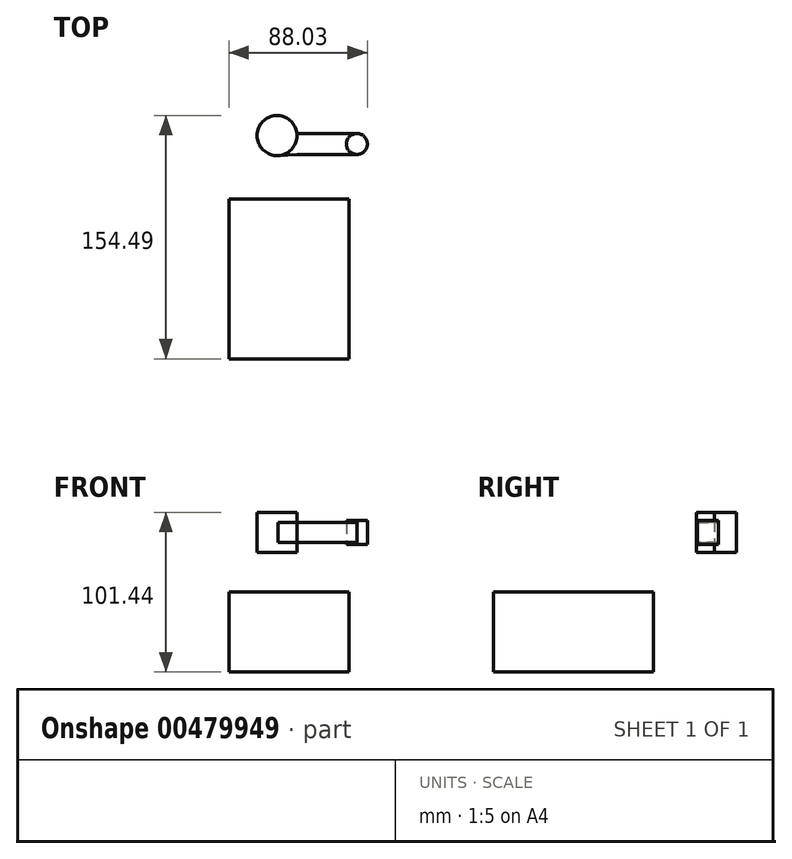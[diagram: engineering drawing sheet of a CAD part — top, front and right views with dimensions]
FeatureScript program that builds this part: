
annotation { "Feature Type Name" : "Feature", "Feature Type Description" : "" }
export const myFeature = defineFeature(function(context is Context, id is Id, definition is map)
    precondition{}
    {
        {
            var Q0;
            Q0=qCreatedBy(makeId("Front.planeOp"),FACE);
            var sketch = newSketch(context, id + "F0", { "sketchPlane" : qUnion([Q0])});
            skLineSegment(sketch, "E0.bottom", {"start": v(-76.2, -25.24) * mm, "end": v(0, -25.24) * mm});
            skLineSegment(sketch, "E0.top", {"start": v(-76.2, -76.04) * mm, "end": v(0, -76.04) * mm});
            skLineSegment(sketch, "E0.left", {"start": v(-76.2, -25.24) * mm, "end": v(-76.2, -76.04) * mm});
            skLineSegment(sketch, "E0.right", {"start": v(0, -25.24) * mm, "end": v(0, -76.04) * mm});
            skSolve(sketch);
        }
        {
            var Q0;
            Q0 = qSketchRegion(id + "F0", true);
            extrude(context, id + "F1", {"entities" : qUnion([Q0]), "depth" : 101.6 * mm});
        }
        {
            var Q0;
            Q0=qCreatedBy(makeId("Top.planeOp"),FACE);
            var sketch = newSketch(context, id + "F2", { "sketchPlane" : qUnion([Q0])});
            skCircle(sketch, "E1", {"center": v(-45.57, 40.19) * mm, "radius": 12.7 * mm});
            skLineSegment(sketch, "E2.bottom", {"start": v(-32.93, 41.47) * mm, "end": v(5.17, 41.47) * mm});
            skLineSegment(sketch, "E2.top", {"start": v(-32.93, 28.15) * mm, "end": v(5.17, 28.15) * mm});
            skLineSegment(sketch, "E2.left", {"start": v(-32.93, 41.47) * mm, "end": v(-32.93, 28.15) * mm});
            skLineSegment(sketch, "E2.right", {"start": v(5.17, 41.47) * mm, "end": v(5.17, 28.15) * mm});
            skLineSegment(sketch, "E3", {"start": v(-32.93, 28.15) * mm, "end": v(-44.88, 27.5) * mm});
            skCircle(sketch, "E4", {"center": v(5.17, 34.81) * mm, "radius": 6.66 * mm});
            skSolve(sketch);
        }
        {
            var Q0;
            {var subQ1=sQuery(id+"F2.wireOp",EDGE,"E1");var subQ3=makeQuery(id+"F2.imprint","INTERSECT",VERTEX,{"derivedFrom":[subQ1,sQuery(id+"F2.wireOp",EDGE,"E3")]});Q0=makeQuery(id+"F2.imprint","IMPRINT",FACE,{"disambiguationData":[TD([[makeQuery(id+"F2.imprint","IMPRINT",EDGE,{"disambiguationData":[TD([[subQ3,-1.0]])],"derivedFrom":subQ1}),1.0]])]});}
            var Q1;
            {var subQ0=sQuery(id+"F2.wireOp",EDGE,"E2.right");Q1=makeQuery(id+"F2.imprint","IMPRINT",FACE,{"disambiguationData":[TD([[makeQuery(id+"F2.imprint","IMPRINT",EDGE,{"derivedFrom":subQ0}),1.0]])]});}
            var Q2;
            {var subQ0=sQuery(id+"F2.wireOp",EDGE,"E2.right");Q2=makeQuery(id+"F2.imprint","IMPRINT",FACE,{"disambiguationData":[TD([[makeQuery(id+"F2.imprint","IMPRINT",EDGE,{"derivedFrom":subQ0}),-1.0]])]});}
            extrude(context, id + "F3", {"entities" : qUnion([Q0, Q1, Q2]), "depth" : 25.4 * mm});
        }
        {
            var Q0;
            {var subQ4=sQuery(id+"F2.wireOp",EDGE,"E2.bottom");Q0=makeQuery(id+"F2.imprint","IMPRINT",FACE,{"disambiguationData":[TD([[makeQuery(id+"F2.imprint","IMPRINT",EDGE,{"derivedFrom":subQ4}),-1.0]])]});}
            var Q1;
            {var subQ0=sQuery(id+"F2.wireOp",EDGE,"E3");Q1=makeQuery(id+"F2.imprint","IMPRINT",FACE,{"disambiguationData":[TD([[makeQuery(id+"F2.imprint","IMPRINT",EDGE,{"derivedFrom":subQ0}),-1.0]])]});}
            extrude(context, id + "F4", {"entities" : qUnion([Q0, Q1]), "depth" : 19.05 * mm});
        }
        {
            var Q0;
            Q0=makeQuery(id+"F4.opExtrude","CAP_FACE",FACE,{"disambiguationData":[OSD([sQuery(id+"F2.wireOp",EDGE,"E1"),sQuery(id+"F2.wireOp",EDGE,"E2.bottom"),sQuery(id+"F2.wireOp",EDGE,"E2.top"),sQuery(id+"F2.wireOp",EDGE,"E3"),sQuery(id+"F2.wireOp",EDGE,"E4")])],"isStart":true});
            extrude(context, id + "F5", {"entities" : qUnion([Q0]), "operationType" : NewBodyOperationType.REMOVE, "oppositeDirection" : true, "depth" : 6.35 * mm});
        }
        {
            var Q0;
            Q0=makeQuery(id+"F3.opExtrude","CAP_FACE",FACE,{"disambiguationData":[OSD([sQuery(id+"F2.wireOp",EDGE,"E4")])],"isStart":false});
            extrude(context, id + "F6", {"entities" : qUnion([Q0]), "operationType" : NewBodyOperationType.REMOVE, "oppositeDirection" : true, "depth" : 5.08 * mm});
        }
        {
            var Q0;
            Q0=makeQuery(id+"F3.opExtrude","CAP_FACE",FACE,{"disambiguationData":[OSD([sQuery(id+"F2.wireOp",EDGE,"E4")])],"isStart":true});
            extrude(context, id + "F7", {"entities" : qUnion([Q0]), "operationType" : NewBodyOperationType.REMOVE, "oppositeDirection" : true, "depth" : 5.08 * mm});
        }
    });
